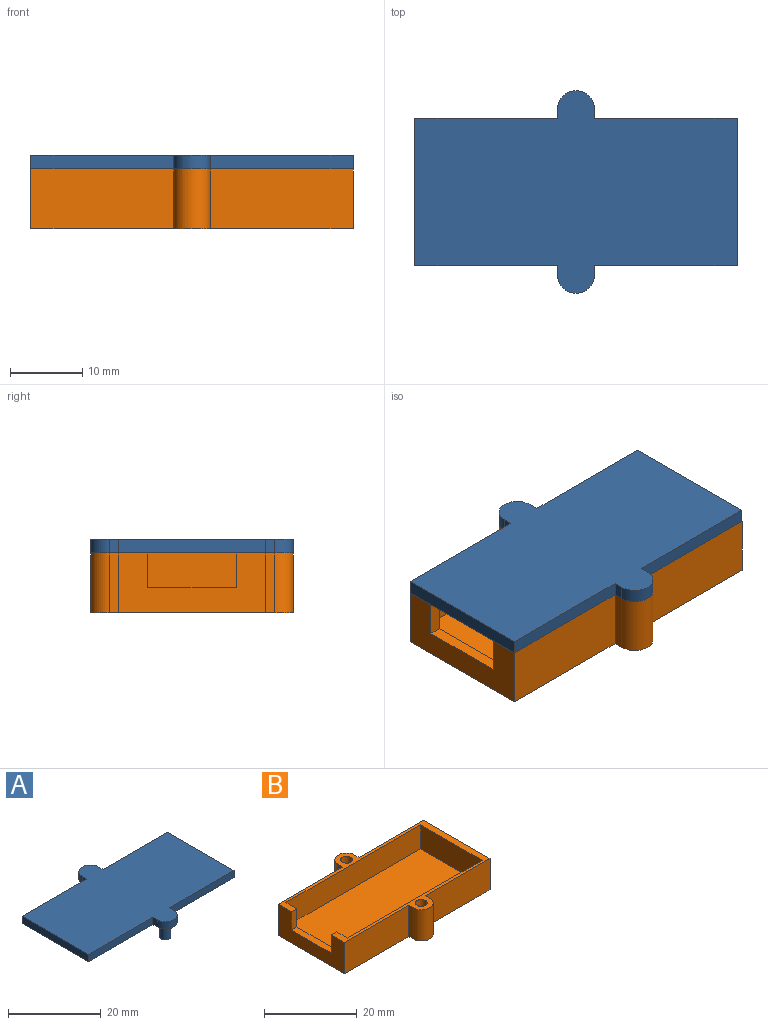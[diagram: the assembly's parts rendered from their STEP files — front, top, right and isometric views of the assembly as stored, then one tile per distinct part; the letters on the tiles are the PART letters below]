
ASSEMBLY  parts=2 mates=1
PART A: 18 faces, bbox 44.5x27.9x5.7 mm
  f0: plane 19.69x1.91mm, normal (0,1,0), area 37.5mm2, adj f1,f11,f12,f13
  f1: plane 20.32x1.91mm, normal (-1,0,0), area 38.7mm2, adj f0,f2,f12,f13
  f2: plane 19.69x1.91mm, normal (0,-1,0), area 37.5mm2, adj f1,f3,f12,f13
  f3: plane 1.91x1.27mm, normal (-1,0,0), area 2.4mm2, adj f2,f4,f12,f13
  f4: cylinder r=2.54mm len=5.08mm, axis (0,0,-1), area 15.2mm2, adj f3,f5,f12,f13
  f5: plane 1.91x1.27mm, normal (1,0,0), area 2.4mm2, adj f4,f6,f12,f13
  f6: plane 19.69x1.91mm, normal (0,-1,0), area 37.5mm2, adj f5,f7,f12,f13
  f7: plane 20.32x1.91mm, normal (1,0,0), area 38.7mm2, adj f6,f8,f12,f13
  f8: plane 19.69x1.91mm, normal (0,1,0), area 37.5mm2, adj f7,f9,f12,f13
  f9: plane 1.91x1.27mm, normal (1,0,0), area 2.4mm2, adj f8,f10,f12,f13
  f10: cylinder r=2.54mm len=5.08mm, axis (0,0,-1), area 15.2mm2, adj f9,f11,f12,f13
  f11: plane 1.91x1.27mm, normal (-1,0,0), area 2.4mm2, adj f0,f10,f12,f13
  f12: plane 44.45x27.94mm, normal (0,0,1), area 936.4mm2, adj f0,f1,f2,f3,f4,f5,f6,f7
  f13: plane 44.45x27.94mm, normal (0,0,-1), area 927.2mm2, adj f0,f1,f2,f3,f4,f5,f6,f7
  f14: cylinder r=1.21mm len=3.81mm, axis (0,0,1), area 28.9mm2, adj f13,f15
  f15: plane 2.41x2.41mm, normal (0,0,-1), area 4.6mm2, adj f14
  f16: cylinder r=1.21mm len=3.81mm, axis (0,0,1), area 28.9mm2, adj f13,f17
  f17: plane 2.41x2.41mm, normal (0,0,-1), area 4.6mm2, adj f16
PART B: 24 faces, bbox 44.5x27.9x8.3 mm
  f0: plane 41.15x18.8mm, normal (0,0,1), area 773.4mm2, adj f18,f19,f20,f21
  f1: plane 19.69x8.26mm, normal (0,1,0), area 162.5mm2, adj f2,f13,f15,f22
  f2: plane 20.32x8.26mm, normal (-1,0,0), area 108.9mm2, adj f1,f3,f15,f16,f17,f22,f23
  f3: plane 19.69x8.26mm, normal (0,-1,0), area 162.5mm2, adj f2,f4,f15,f22
  f4: plane 8.26x1.27mm, normal (-1,0,0), area 10.5mm2, adj f3,f5,f15,f22
  f5: cylinder r=2.54mm len=8.26mm, axis (0,0,-1), area 65.9mm2, adj f4,f6,f15,f22
  f6: plane 8.26x1.27mm, normal (1,0,0), area 10.5mm2, adj f5,f7,f15,f22
  f7: plane 19.69x8.26mm, normal (0,-1,0), area 162.5mm2, adj f6,f8,f15,f22
  f8: plane 20.32x8.26mm, normal (1,0,0), area 167.7mm2, adj f7,f9,f15,f22
  f9: plane 19.69x8.26mm, normal (0,1,0), area 162.5mm2, adj f8,f10,f15,f22
  f10: plane 8.26x1.27mm, normal (1,0,0), area 10.5mm2, adj f9,f11,f15,f22
  f11: cylinder r=2.54mm len=8.26mm, axis (0,0,-1), area 65.9mm2, adj f10,f13,f15,f22
  f12: cylinder r=1.27mm len=8.26mm, axis (0,0,-1), area 65.9mm2, adj f15,f22
  f13: plane 8.26x1.27mm, normal (-1,0,0), area 10.5mm2, adj f1,f11,f15,f22
  f14: cylinder r=1.27mm len=8.26mm, axis (0,0,-1), area 65.9mm2, adj f15,f22
  f15: plane 44.45x27.94mm, normal (0,0,-1), area 926.3mm2, adj f1,f2,f3,f4,f5,f6,f7,f8
  f16: plane 4.83x1.65mm, normal (0,1,0), area 8mm2, adj f2,f18,f22,f23
  f17: plane 4.83x1.65mm, normal (0,-1,0), area 8mm2, adj f2,f18,f22,f23
  f18: plane 18.8x6.35mm, normal (1,0,0), area 60.5mm2, adj f0,f16,f17,f19,f21,f22,f23
  f19: plane 41.15x6.35mm, normal (0,-1,0), area 261.3mm2, adj f0,f18,f20,f22
  f20: plane 18.8x6.35mm, normal (-1,0,0), area 119.4mm2, adj f0,f19,f21,f22
  f21: plane 41.15x6.35mm, normal (0,1,0), area 261.3mm2, adj f0,f18,f20,f22
  f22: plane 44.45x27.94mm, normal (0,0,1), area 132.7mm2, adj f1,f2,f3,f4,f5,f6,f7,f8
  f23: plane 12.19x1.65mm, normal (0,0,1), area 20.1mm2, adj f2,f16,f17,f18
PLACE A t=(-4.89,1.37,-1.85)mm
PLACE B t=(-4.89,1.37,-1.85)mm
MATE cylindrical A.f4 <-> B.f5  axis (0,0,1) through (17.33,0.1,4.5)mm
